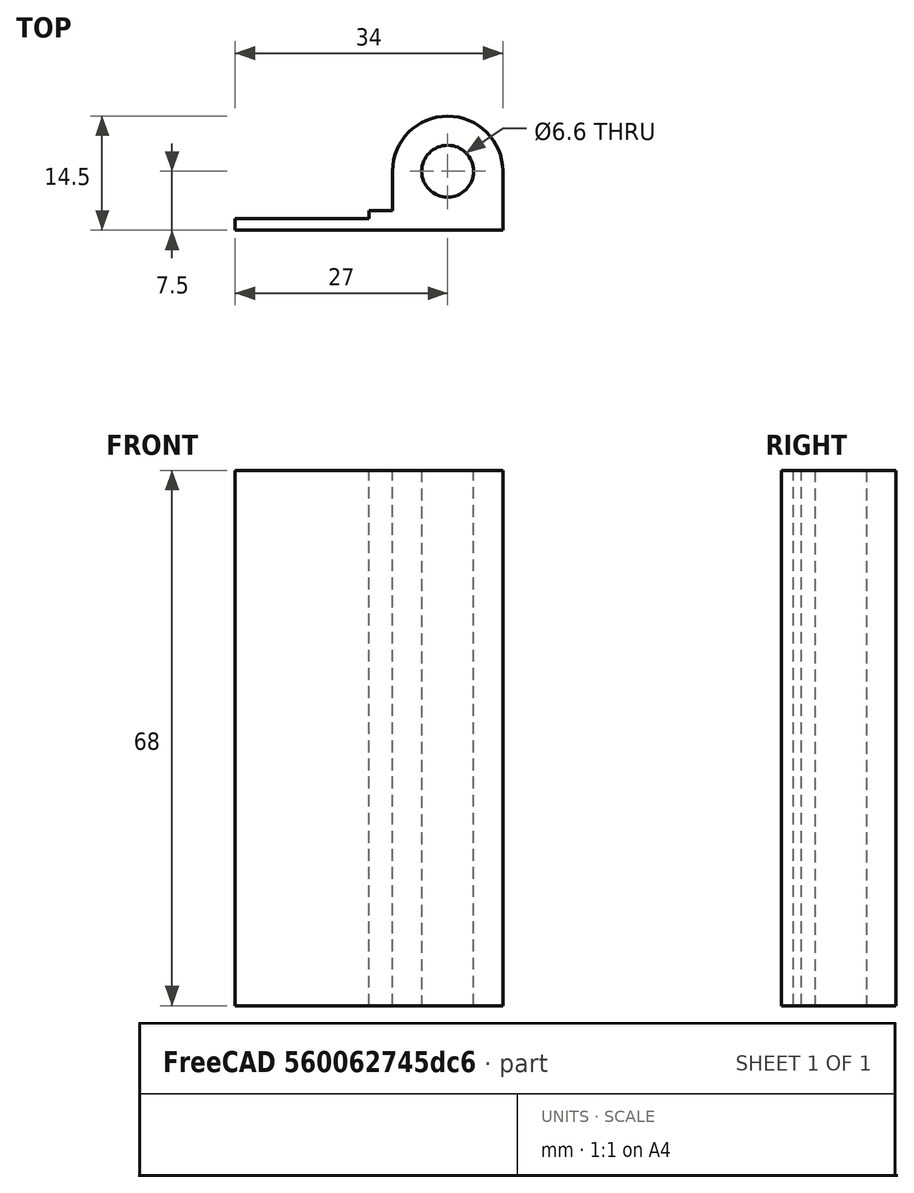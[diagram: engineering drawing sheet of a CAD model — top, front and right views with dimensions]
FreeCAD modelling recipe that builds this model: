
FCSTD DOCUMENT  (FreeCAD 0.18R16110 (Git))
Label: carrier3_6.5
License: All rights reserved
LicenseURL: http://en.wikipedia.org/wiki/All_rights_reserved
objects: Sketcher::SketchObject×1, PartDesign::Pad×1, PartDesign::Body×1
note: 4 computed .brp shape members not serialized (recipe doc carries the construction recipe); baked Part::Feature solids carry a one-line shape summary decoded from their .brp

FEATURE [Sketcher::SketchObject] Sketch
  MapMode = 5
  Support = -> [XY_Plane]
  sketch-geometry (9):
    g0: LineSegment StartX=17 StartY=1.5 StartZ=0 EndX=0 EndY=1.5 EndZ=0
    g1: LineSegment StartX=0 StartY=1.5 StartZ=0 EndX=0 EndY=0 EndZ=0
    g2: LineSegment StartX=0 StartY=0 StartZ=0 EndX=34 EndY=0 EndZ=0
    g3: LineSegment StartX=34 StartY=0 StartZ=0 EndX=34 EndY=7.49999 EndZ=0
    g4: ArcOfCircle CenterX=27 CenterY=7.5 CenterZ=0 NormalX=0 NormalY=0 NormalZ=1 AngleXU=0 Radius=7 StartAngle=6.28318 EndAngle=9.42478
    g5: Circle CenterX=27 CenterY=7.5 CenterZ=0 NormalX=0 NormalY=0 NormalZ=1 AngleXU=0 Radius=3.3
    g6: LineSegment StartX=17 StartY=1.5 StartZ=0 EndX=17 EndY=2.5 EndZ=0
    g7: LineSegment StartX=17 StartY=2.5 StartZ=0 EndX=20 EndY=2.5 EndZ=0
    g8: LineSegment StartX=20 StartY=2.5 StartZ=0 EndX=20 EndY=7.50001 EndZ=0
  constraints (26):
    c: Coincident(g0,g1)
    c: Coincident(g1,g2)
    c: Coincident(g2,g3)
    c: Radius(g4) = 7
    c: Radius(g5) = 3.3
    c: Coincident(g4,g5)
    c: Angle(g4) = 3.14159
    c: Horizontal(g2)
    c: Horizontal(g0)
    c: Vertical(g1)
    c: Coincident(g1,g-1)
    c: DistanceY(g1,g1) = 1.5
    c: DistanceX(g0,g0) = 17
    c: Vertical(g6)
    c: Horizontal(g7)
    c: Distance(g7,g2) = 2.5
    c: DistanceX(g7,g7) = 3
    c: Coincident(g6,g7)
    c: Coincident(g6,g0)
    c: Vertical(g3)
    c: Coincident(g3,g4)
    c: Coincident(g4,g8)
    c: Coincident(g7,g8)
    c: Vertical(g8)
    c: Distance(g4,g2) = 7.5
    c: Distance(g2,g1) = 34
FEATURE [PartDesign::Pad] Pad
  Length = 68
  Length2 = 100
  Profile = -> Sketch
  Type = 0
FEATURE [PartDesign::Body] Body
  Group = -> [Sketch,Pad]
  Origin = -> Origin
  Tip = -> Pad
